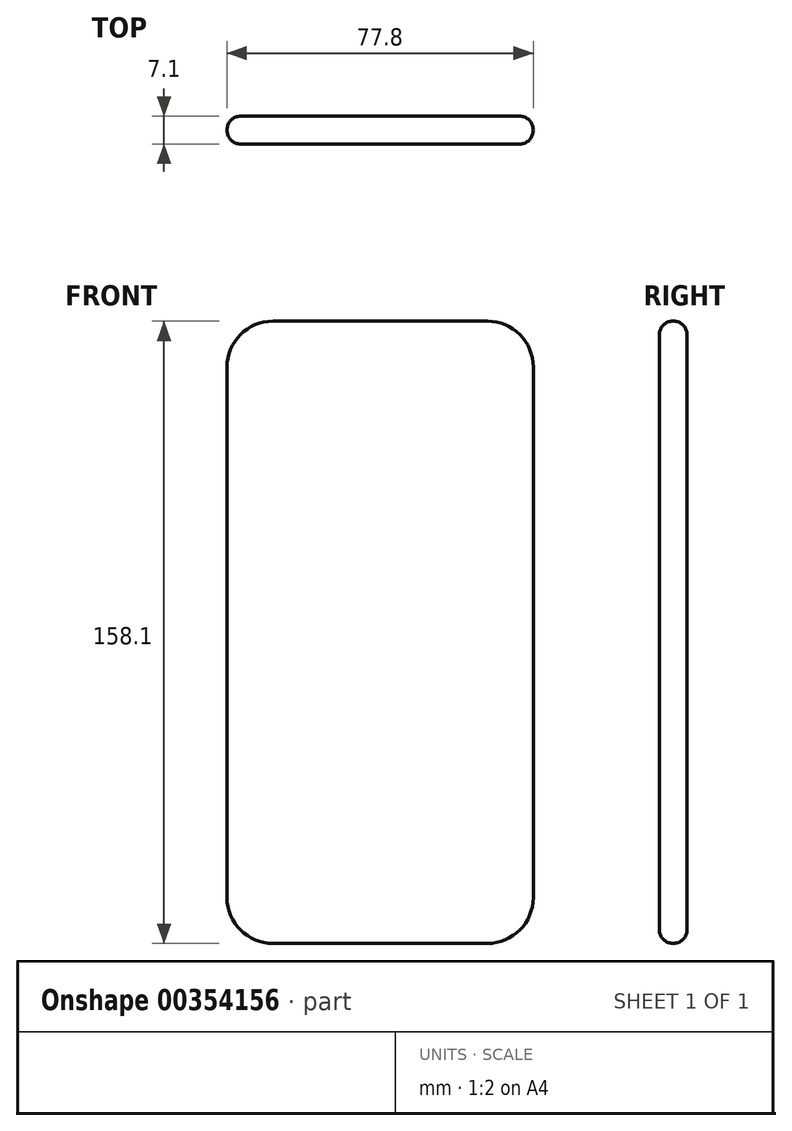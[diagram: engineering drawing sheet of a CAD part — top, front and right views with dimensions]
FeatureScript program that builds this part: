
annotation { "Feature Type Name" : "Feature", "Feature Type Description" : "" }
export const myFeature = defineFeature(function(context is Context, id is Id, definition is map)
    precondition{}
    {
        {
            var Q0;
            Q0=qCreatedBy(makeId("Front.planeOp"),FACE);
            var sketch = newSketch(context, id + "F0", { "sketchPlane" : qUnion([Q0])});
            skLineSegment(sketch, "E0.bottom", {"start": v(-27.22, 79.05) * mm, "end": v(27.22, 79.05) * mm});
            skLineSegment(sketch, "E0.top", {"start": v(-27.22, -79.05) * mm, "end": v(27.22, -79.05) * mm});
            skLineSegment(sketch, "E0.left", {"start": v(-38.9, 67.37) * mm, "end": v(-38.9, -67.37) * mm});
            skLineSegment(sketch, "E0.right", {"start": v(38.9, 67.37) * mm, "end": v(38.9, -67.37) * mm});
            skPoint(sketch, "E1.visualSharp", {"position": v(-38.9, 79.05) * mm});
            skArc(sketch, "E1.filletArc", {"start": v(-27.22, 79.05) * mm, "mid": v(-35.48, 75.63) * mm, "end": v(-38.9, 67.37) * mm});
            skPoint(sketch, "E2.visualSharp", {"position": v(38.9, 79.05) * mm});
            skArc(sketch, "E2.filletArc", {"start": v(38.9, 67.37) * mm, "mid": v(35.48, 75.63) * mm, "end": v(27.22, 79.05) * mm});
            skPoint(sketch, "E3.visualSharp", {"position": v(38.9, -79.05) * mm});
            skArc(sketch, "E3.filletArc", {"start": v(27.22, -79.05) * mm, "mid": v(35.48, -75.63) * mm, "end": v(38.9, -67.37) * mm});
            skPoint(sketch, "E4.visualSharp", {"position": v(-38.9, -79.05) * mm});
            skArc(sketch, "E4.filletArc", {"start": v(-38.9, -67.37) * mm, "mid": v(-35.48, -75.63) * mm, "end": v(-27.22, -79.05) * mm});
            skSolve(sketch);
        }
        {
            var Q0;
            Q0=makeQuery(id+"F0.imprint","IMPRINT",FACE,{"disambiguationData":[TD([[makeQuery(id+"F0.imprint","IMPRINT",EDGE,{"derivedFrom":sQuery(id+"F0.wireOp",EDGE,"E0.bottom")}),-1.0]])]});
            extrude(context, id + "F1", {"entities" : qUnion([Q0]), "oppositeDirection" : true, "depth" : 7.1 * mm});
        }
        {
            var Q0;
            Q0=makeQuery(id+"F1.opExtrude","CAP_FACE",FACE,{"disambiguationData":[OSD([sQuery(id+"F0.wireOp",EDGE,"E0.bottom"),sQuery(id+"F0.wireOp",EDGE,"E0.top"),sQuery(id+"F0.wireOp",EDGE,"E0.left"),sQuery(id+"F0.wireOp",EDGE,"E0.right"),sQuery(id+"F0.wireOp",EDGE,"E1.filletArc"),sQuery(id+"F0.wireOp",EDGE,"E2.filletArc"),sQuery(id+"F0.wireOp",EDGE,"E3.filletArc"),sQuery(id+"F0.wireOp",EDGE,"E4.filletArc")])],"isStart":true});
            var Q1;
            Q1=makeQuery(id+"F1.opExtrude","CAP_FACE",FACE,{"disambiguationData":[OSD([sQuery(id+"F0.wireOp",EDGE,"E0.bottom"),sQuery(id+"F0.wireOp",EDGE,"E0.top"),sQuery(id+"F0.wireOp",EDGE,"E0.left"),sQuery(id+"F0.wireOp",EDGE,"E0.right"),sQuery(id+"F0.wireOp",EDGE,"E1.filletArc"),sQuery(id+"F0.wireOp",EDGE,"E2.filletArc"),sQuery(id+"F0.wireOp",EDGE,"E3.filletArc"),sQuery(id+"F0.wireOp",EDGE,"E4.filletArc")])],"isStart":false});
            fillet(context, id + "F2", {"entities" : qUnion([Q0, Q1]), "radius" : 3.5 * mm, "tangentPropagation" : true, "allowEdgeOverflow" : false});
        }
    });
